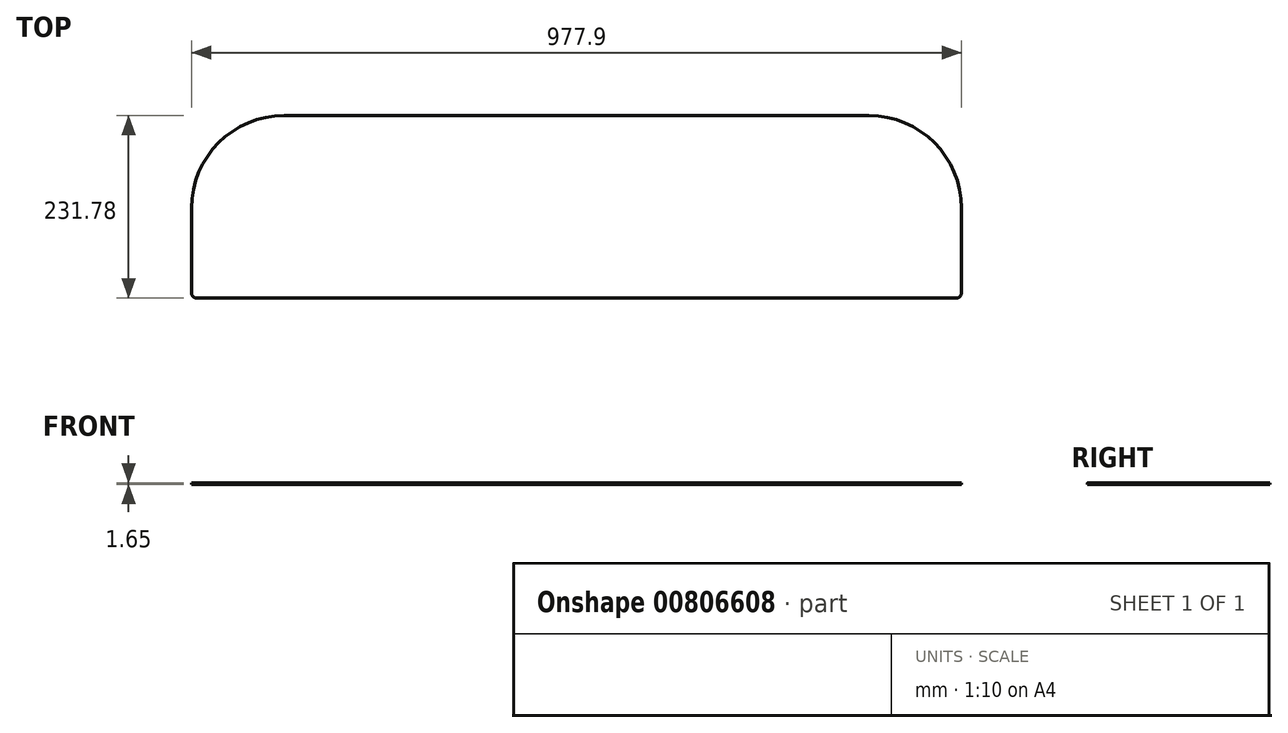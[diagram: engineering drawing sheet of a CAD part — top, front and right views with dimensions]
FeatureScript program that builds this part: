
annotation { "Feature Type Name" : "Feature", "Feature Type Description" : "" }
export const myFeature = defineFeature(function(context is Context, id is Id, definition is map)
    precondition{}
    {
        {
            var Q0;
            Q0=qCreatedBy(makeId("Top.planeOp"),FACE);
            var sketch = newSketch(context, id + "F0", { "sketchPlane" : qUnion([Q0])});
            skLineSegment(sketch, "E0.bottom", {"start": v(6.35, 0) * mm, "end": v(971.55, 0) * mm});
            skLineSegment(sketch, "E0.top", {"start": v(117.47, 231.78) * mm, "end": v(860.42, 231.78) * mm});
            skLineSegment(sketch, "E0.left", {"start": v(0, 6.35) * mm, "end": v(0, 114.3) * mm});
            skLineSegment(sketch, "E0.right", {"start": v(977.9, 6.35) * mm, "end": v(977.9, 114.3) * mm});
            skPoint(sketch, "E1.visualSharp", {"position": v(0, 231.78) * mm});
            skArc(sketch, "E1.filletArc", {"start": v(117.47, 231.78) * mm, "mid": v(34.4, 197.37) * mm, "end": v(0, 114.3) * mm});
            skPoint(sketch, "E2.visualSharp", {"position": v(977.9, 231.78) * mm});
            skArc(sketch, "E2.filletArc", {"start": v(977.9, 114.3) * mm, "mid": v(943.5, 197.37) * mm, "end": v(860.42, 231.78) * mm});
            skPoint(sketch, "E3.visualSharp", {"position": v(977.9, 0) * mm});
            skArc(sketch, "E3.filletArc", {"start": v(971.55, 0) * mm, "mid": v(976.04, 1.86) * mm, "end": v(977.9, 6.35) * mm});
            skPoint(sketch, "E4.visualSharp", {"position": v(0, 0) * mm});
            skArc(sketch, "E4.filletArc", {"start": v(0, 6.35) * mm, "mid": v(1.86, 1.86) * mm, "end": v(6.35, 0) * mm});
            skSolve(sketch);
        }
        {
            var Q0;
            Q0 = qSketchRegion(id + "F0", true);
            extrude(context, id + "F1", {"entities" : qUnion([Q0]), "depth" : 1.65 * mm, "offsetDistance" : 25.4 * mm});
        }
    });
